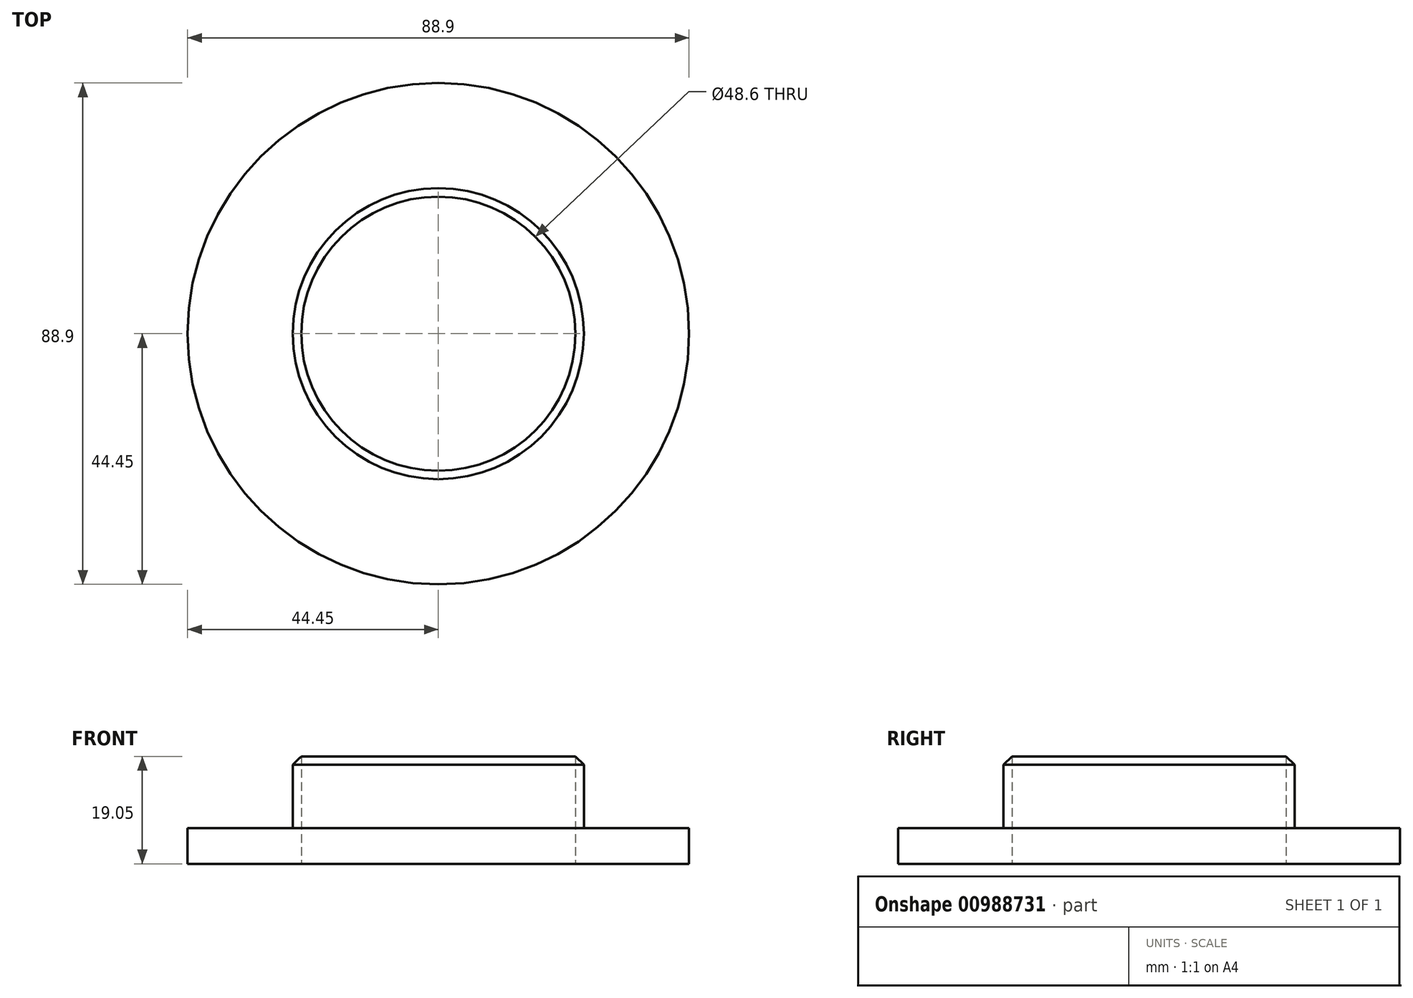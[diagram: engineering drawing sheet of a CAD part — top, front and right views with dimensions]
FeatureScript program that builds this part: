
annotation { "Feature Type Name" : "Feature", "Feature Type Description" : "" }
export const myFeature = defineFeature(function(context is Context, id is Id, definition is map)
    precondition{}
    {
        {
            var Q0;
            Q0=qCreatedBy(makeId("Front.planeOp"),FACE);
            var sketch = newSketch(context, id + "F0", { "sketchPlane" : qUnion([Q0])});
            skLineSegment(sketch, "E0", {"start": v(0, 0) * mm, "end": v(0, 27.15) * mm, "construction": true});
            skLineSegment(sketch, "E1", {"start": v(24.3, 31.83) * mm, "end": v(24.3, 12.78) * mm});
            skLineSegment(sketch, "E2", {"start": v(24.3, 12.78) * mm, "end": v(44.45, 12.78) * mm});
            skLineSegment(sketch, "E3", {"start": v(44.45, 12.78) * mm, "end": v(44.45, 19.13) * mm});
            skLineSegment(sketch, "E4", {"start": v(44.45, 19.13) * mm, "end": v(25.8, 19.13) * mm});
            skLineSegment(sketch, "E5", {"start": v(25.8, 19.13) * mm, "end": v(25.8, 30.33) * mm});
            skLineSegment(sketch, "E6", {"start": v(25.8, 30.33) * mm, "end": v(24.3, 31.83) * mm});
            skSolve(sketch);
        }
        {
            var Q0;
            Q0=makeQuery(id+"F0.imprint","IMPRINT",FACE,{"disambiguationData":[TD([[makeQuery(id+"F0.imprint","IMPRINT",EDGE,{"derivedFrom":sQuery(id+"F0.wireOp",EDGE,"E1")}),1.0]])]});
            var Q1;
            Q1=sQuery(id+"F0.wireOp",EDGE,"E0");
            revolve(context, id + "F1", {"surfaceOperationType" : NewSurfaceOperationType.NEW, "entities" : qUnion([Q0]), "axis" : qUnion([Q1]), "revolveType" : RevolveType.FULL});
        }
    });
